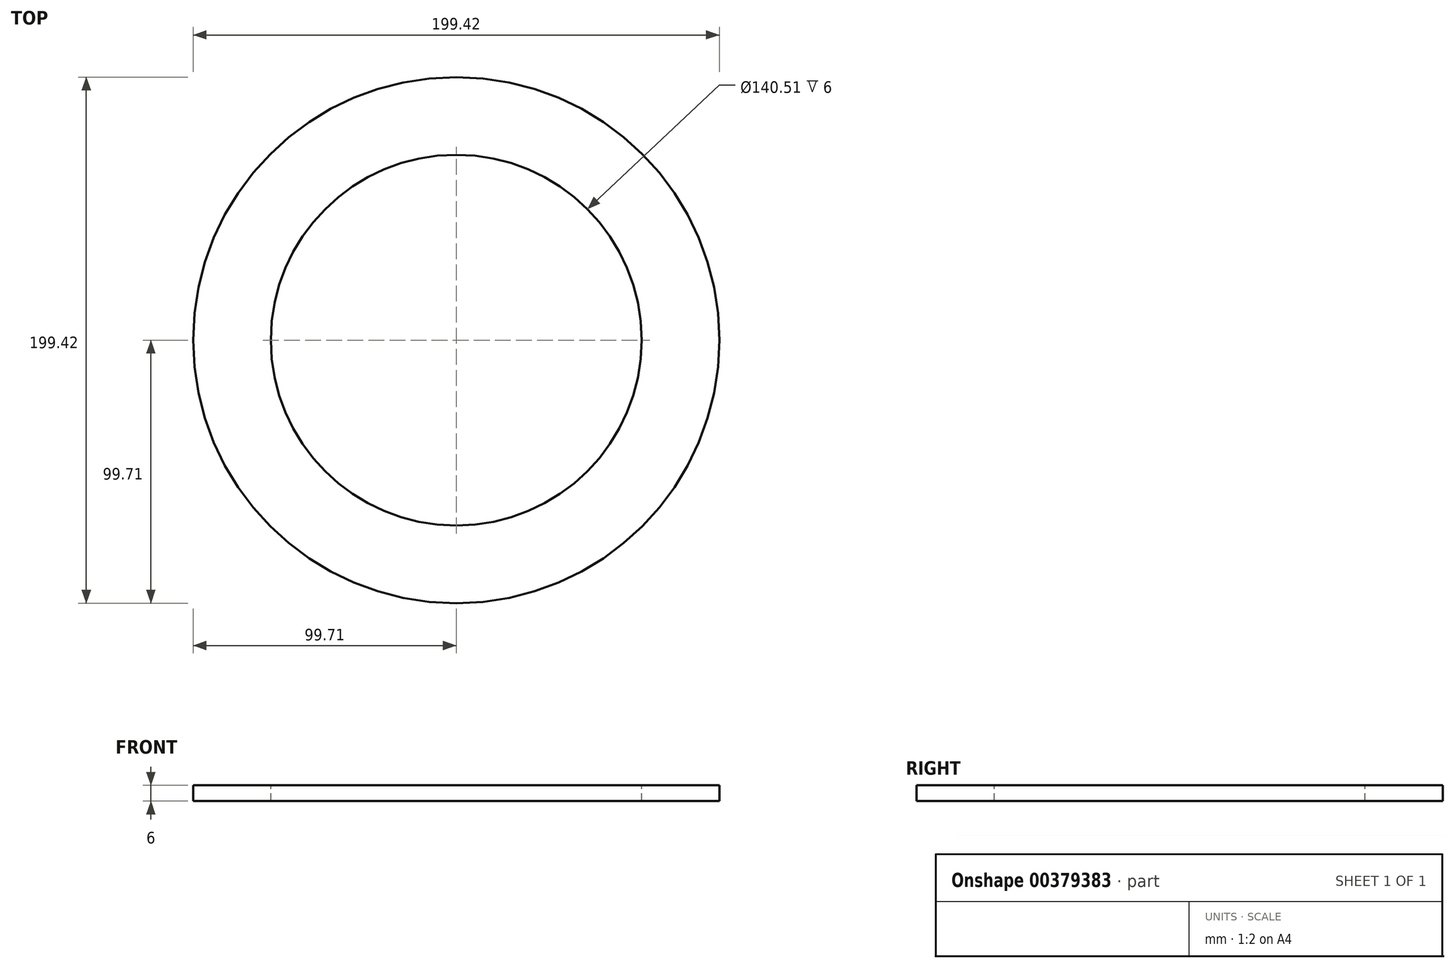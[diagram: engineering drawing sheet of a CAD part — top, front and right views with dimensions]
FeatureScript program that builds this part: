
annotation { "Feature Type Name" : "Feature", "Feature Type Description" : "" }
export const myFeature = defineFeature(function(context is Context, id is Id, definition is map)
    precondition{}
    {
        {
            var Q0;
            Q0=qCreatedBy(makeId("Top.planeOp"),FACE);
            var sketch = newSketch(context, id + "F0", { "sketchPlane" : qUnion([Q0])});
            skCircle(sketch, "E0", {"center": v(0, 0) * mm, "radius": 99.7 * mm});
            skCircle(sketch, "E1", {"center": v(0, 0) * mm, "radius": 70.25 * mm});
            skSolve(sketch);
        }
        {
            var Q0;
            Q0=makeQuery(id+"F0.imprint","IMPRINT",FACE,{"disambiguationData":[TD([[makeQuery(id+"F0.imprint","IMPRINT",EDGE,{"derivedFrom":sQuery(id+"F0.wireOp",EDGE,"E0")}),1.0]])]});
            extrude(context, id + "F1", {"entities" : qUnion([Q0]), "oppositeDirection" : true, "depth" : 6 * mm});
        }
    });
